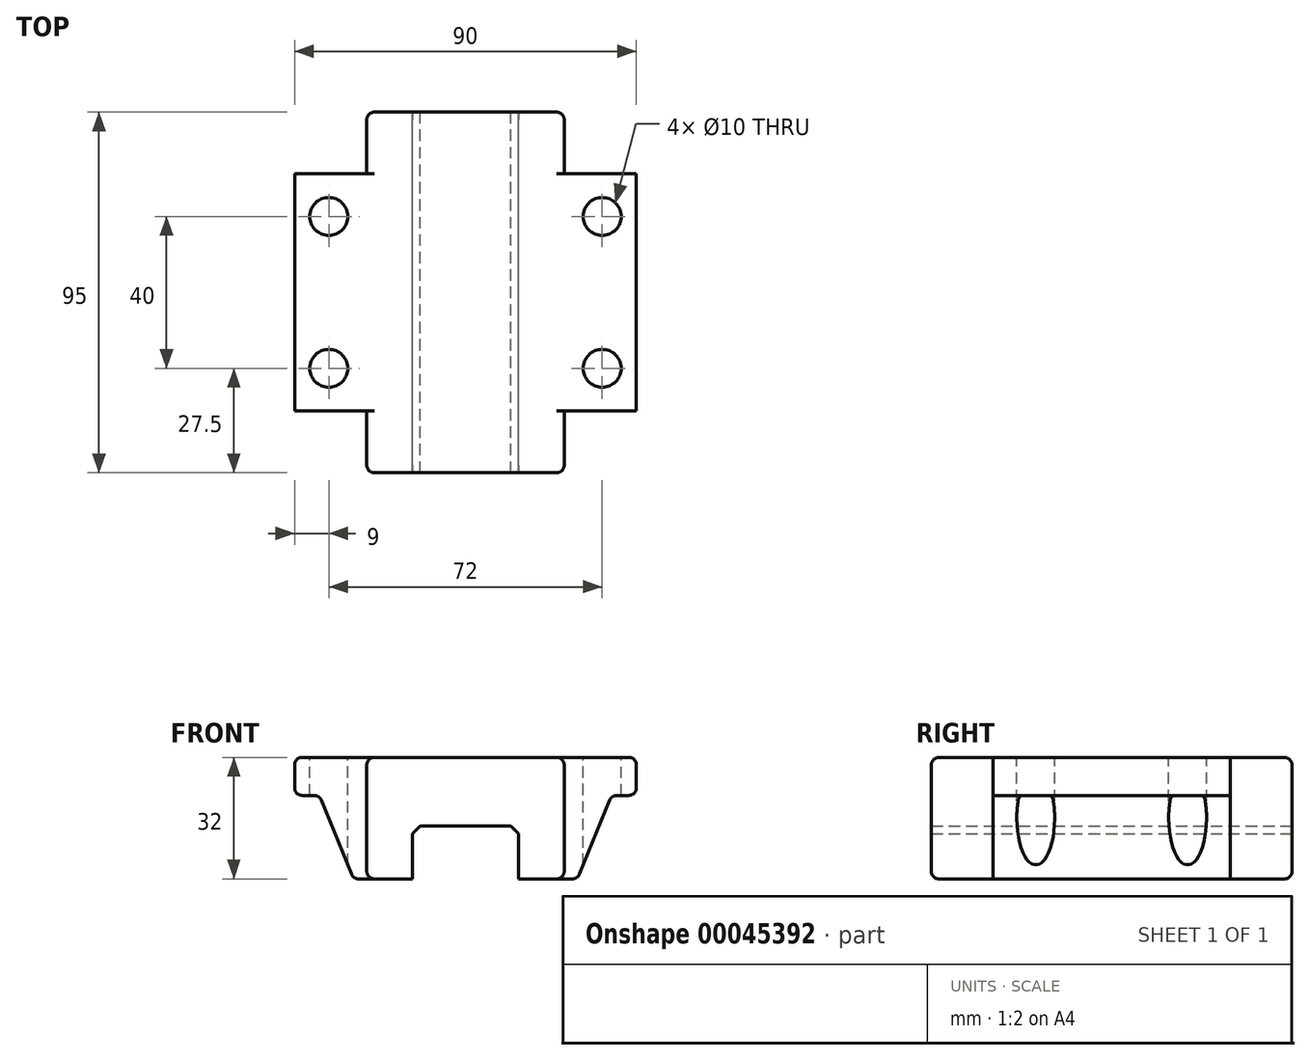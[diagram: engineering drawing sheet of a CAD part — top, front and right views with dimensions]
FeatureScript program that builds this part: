
annotation { "Feature Type Name" : "Feature", "Feature Type Description" : "" }
export const myFeature = defineFeature(function(context is Context, id is Id, definition is map)
    precondition{}
    {
        {
            var Q0;
            Q0=qCreatedBy(makeId("Front.planeOp"),FACE);
            var sketch = newSketch(context, id + "F0", { "sketchPlane" : qUnion([Q0])});
            skLineSegment(sketch, "E0.bottom", {"start": v(-47.43, 10.94) * mm, "end": v(42.57, 10.94) * mm});
            skLineSegment(sketch, "E0.top", {"start": v(-47.43, -21.06) * mm, "end": v(42.57, -21.06) * mm});
            skLineSegment(sketch, "E0.left", {"start": v(-47.43, 10.94) * mm, "end": v(-47.43, -21.06) * mm});
            skLineSegment(sketch, "E0.right", {"start": v(42.57, 10.94) * mm, "end": v(42.57, -21.06) * mm});
            skSolve(sketch);
        }
        {
            var Q0;
            Q0=qSketchRegion(id+"F0",true);
            extrude(context, id + "F1", {"entities" : qUnion([Q0]), "depth" : 65.2 * mm});
        }
        {
            var Q0;
            Q0=makeQuery(id+"F1.opExtrude","CAP_FACE",FACE,{"disambiguationData":[OSD([sQuery(id+"F0.wireOp",EDGE,"E0.bottom"),sQuery(id+"F0.wireOp",EDGE,"E0.top"),sQuery(id+"F0.wireOp",EDGE,"E0.left"),sQuery(id+"F0.wireOp",EDGE,"E0.right")])],"isStart":false});
            var sketch = newSketch(context, id + "F2", { "sketchPlane" : qUnion([Q0])});
            skLineSegment(sketch, "E1.bottom", {"start": v(-45.43, 10.94) * mm, "end": v(40.57, 10.94) * mm});
            skLineSegment(sketch, "E1.top", {"start": v(-45.43, 0.94) * mm, "end": v(-42.27, 0.94) * mm});
            skLineSegment(sketch, "E1.left", {"start": v(-47.43, 8.94) * mm, "end": v(-47.43, 2.94) * mm});
            skLineSegment(sketch, "E1.right", {"start": v(42.57, 8.94) * mm, "end": v(42.57, 2.94) * mm});
            skLineSegment(sketch, "E2.top", {"start": v(-30.59, -21.06) * mm, "end": v(25.73, -21.06) * mm});
            skLineSegment(sketch, "E3", {"start": v(-40.42, -0.3) * mm, "end": v(-32.44, -19.82) * mm});
            skLineSegment(sketch, "E4", {"start": v(27.58, -19.82) * mm, "end": v(35.56, -0.3) * mm});
            skLineSegment(sketch, "E5.trimOffspring", {"start": v(37.41, 0.94) * mm, "end": v(40.57, 0.94) * mm});
            skPoint(sketch, "E6.visualSharp", {"position": v(42.57, 0.94) * mm});
            skArc(sketch, "E6.filletArc", {"start": v(40.57, 0.94) * mm, "mid": v(41.98, 1.53) * mm, "end": v(42.57, 2.94) * mm});
            skPoint(sketch, "E7.visualSharp", {"position": v(42.57, 10.94) * mm});
            skArc(sketch, "E7.filletArc", {"start": v(42.57, 8.94) * mm, "mid": v(41.98, 10.36) * mm, "end": v(40.57, 10.94) * mm});
            skPoint(sketch, "E8.visualSharp", {"position": v(36.07, 0.94) * mm});
            skArc(sketch, "E8.filletArc", {"start": v(37.41, 0.94) * mm, "mid": v(36.3, 0.6) * mm, "end": v(35.56, -0.3) * mm});
            skPoint(sketch, "E9.visualSharp", {"position": v(27.07, -21.06) * mm});
            skArc(sketch, "E9.filletArc", {"start": v(25.73, -21.06) * mm, "mid": v(26.84, -20.72) * mm, "end": v(27.58, -19.82) * mm});
            skPoint(sketch, "E10.visualSharp", {"position": v(-31.93, -21.06) * mm});
            skArc(sketch, "E10.filletArc", {"start": v(-32.44, -19.82) * mm, "mid": v(-31.7, -20.72) * mm, "end": v(-30.59, -21.06) * mm});
            skPoint(sketch, "E11.visualSharp", {"position": v(-40.93, 0.94) * mm});
            skArc(sketch, "E11.filletArc", {"start": v(-40.42, -0.3) * mm, "mid": v(-41.16, 0.6) * mm, "end": v(-42.27, 0.94) * mm});
            skPoint(sketch, "E12.visualSharp", {"position": v(-47.43, 0.94) * mm});
            skArc(sketch, "E12.filletArc", {"start": v(-47.43, 2.94) * mm, "mid": v(-46.84, 1.53) * mm, "end": v(-45.43, 0.94) * mm});
            skPoint(sketch, "E13.visualSharp", {"position": v(-47.43, 10.94) * mm});
            skArc(sketch, "E13.filletArc", {"start": v(-45.43, 10.94) * mm, "mid": v(-46.84, 10.36) * mm, "end": v(-47.43, 8.94) * mm});
            skSolve(sketch);
        }
        {
            var Q0;
            Q0=qSketchRegion(id+"F2",true);
            extrude(context, id + "F3", {"entities" : qUnion([Q0]), "operationType" : NewBodyOperationType.ADD, "depth" : 25 * mm});
        }
        {
            var Q0;
            Q0=makeQuery(id+"F3.boolean.opBoolean","MERGE",FACE,{"derivedFrom":[makeQuery(id+"F1.opExtrude","SWEPT_FACE",FACE,{"disambiguationData":[OSD([sQuery(id+"F0.wireOp",EDGE,"E0.bottom")])]}),makeQuery(id+"F3.opExtrude","SWEPT_FACE",FACE,{"disambiguationData":[OSD([sQuery(id+"F2.wireOp",EDGE,"E1.bottom")])]})]});
            var sketch = newSketch(context, id + "F4", { "sketchPlane" : qUnion([Q0])});
            skLineSegment(sketch, "E14.bottom", {"start": v(-47.43, 0) * mm, "end": v(42.57, 0) * mm});
            skLineSegment(sketch, "E14.top", {"start": v(-47.43, -65.2) * mm, "end": v(42.57, -65.2) * mm});
            skLineSegment(sketch, "E14.left", {"start": v(-47.43, 0) * mm, "end": v(-47.43, -65.2) * mm});
            skLineSegment(sketch, "E14.right", {"start": v(42.57, 0) * mm, "end": v(42.57, -65.2) * mm});
            skSolve(sketch);
        }
        {
            var Q0;
            Q0=qSketchRegion(id+"F4",true);
            extrude(context, id + "F5", {"entities" : qUnion([Q0]), "operationType" : NewBodyOperationType.REMOVE, "endBound" : BoundingType.THROUGH_ALL, "oppositeDirection" : true, "depth" : 25 * mm});
        }
        {
            var Q0;
            Q0=makeQuery(id+"F3.opExtrude","CAP_FACE",FACE,{"disambiguationData":[OSD([sQuery(id+"F2.wireOp",EDGE,"E1.bottom"),sQuery(id+"F2.wireOp",EDGE,"E1.top"),sQuery(id+"F2.wireOp",EDGE,"E1.left"),sQuery(id+"F2.wireOp",EDGE,"E1.right"),sQuery(id+"F2.wireOp",EDGE,"E2.top"),sQuery(id+"F2.wireOp",EDGE,"E3"),sQuery(id+"F2.wireOp",EDGE,"E4"),sQuery(id+"F2.wireOp",EDGE,"E5.trimOffspring"),sQuery(id+"F2.wireOp",EDGE,"E6.filletArc"),sQuery(id+"F2.wireOp",EDGE,"E7.filletArc"),sQuery(id+"F2.wireOp",EDGE,"E8.filletArc"),sQuery(id+"F2.wireOp",EDGE,"E9.filletArc"),sQuery(id+"F2.wireOp",EDGE,"E10.filletArc"),sQuery(id+"F2.wireOp",EDGE,"E11.filletArc"),sQuery(id+"F2.wireOp",EDGE,"E12.filletArc"),sQuery(id+"F2.wireOp",EDGE,"E13.filletArc")])],"isStart":false});
            extrude(context, id + "F6", {"entities" : qUnion([Q0]), "operationType" : NewBodyOperationType.ADD, "oppositeDirection" : true, "depth" : 62.5 * mm});
        }
        {
            var Q0;
            Q0=makeQuery(id+"F3.opExtrude","CAP_FACE",FACE,{"disambiguationData":[OSD([sQuery(id+"F2.wireOp",EDGE,"E1.bottom"),sQuery(id+"F2.wireOp",EDGE,"E1.top"),sQuery(id+"F2.wireOp",EDGE,"E1.left"),sQuery(id+"F2.wireOp",EDGE,"E1.right"),sQuery(id+"F2.wireOp",EDGE,"E2.top"),sQuery(id+"F2.wireOp",EDGE,"E3"),sQuery(id+"F2.wireOp",EDGE,"E4"),sQuery(id+"F2.wireOp",EDGE,"E5.trimOffspring"),sQuery(id+"F2.wireOp",EDGE,"E6.filletArc"),sQuery(id+"F2.wireOp",EDGE,"E7.filletArc"),sQuery(id+"F2.wireOp",EDGE,"E8.filletArc"),sQuery(id+"F2.wireOp",EDGE,"E9.filletArc"),sQuery(id+"F2.wireOp",EDGE,"E10.filletArc"),sQuery(id+"F2.wireOp",EDGE,"E11.filletArc"),sQuery(id+"F2.wireOp",EDGE,"E12.filletArc"),sQuery(id+"F2.wireOp",EDGE,"E13.filletArc")])],"isStart":false});
            var sketch = newSketch(context, id + "F7", { "sketchPlane" : qUnion([Q0])});
            skLineSegment(sketch, "E15.bottom", {"start": v(-26.43, 10.94) * mm, "end": v(21.57, 10.94) * mm});
            skLineSegment(sketch, "E15.top", {"start": v(-26.43, -21.06) * mm, "end": v(-16.43, -21.06) * mm});
            skLineSegment(sketch, "E15.left", {"start": v(-28.43, 8.94) * mm, "end": v(-28.43, -19.06) * mm});
            skLineSegment(sketch, "E15.right", {"start": v(23.57, 8.94) * mm, "end": v(23.57, -19.06) * mm});
            skPoint(sketch, "E16.visualSharp", {"position": v(-28.43, 10.94) * mm});
            skArc(sketch, "E16.filletArc", {"start": v(-26.43, 10.94) * mm, "mid": v(-27.84, 10.36) * mm, "end": v(-28.43, 8.94) * mm});
            skPoint(sketch, "E17.visualSharp", {"position": v(23.57, 10.94) * mm});
            skArc(sketch, "E17.filletArc", {"start": v(23.57, 8.94) * mm, "mid": v(22.98, 10.36) * mm, "end": v(21.57, 10.94) * mm});
            skPoint(sketch, "E18.visualSharp", {"position": v(23.57, -21.06) * mm});
            skArc(sketch, "E18.filletArc", {"start": v(21.57, -21.06) * mm, "mid": v(22.98, -20.47) * mm, "end": v(23.57, -19.06) * mm});
            skPoint(sketch, "E19.visualSharp", {"position": v(-28.43, -21.06) * mm});
            skArc(sketch, "E19.filletArc", {"start": v(-28.43, -19.06) * mm, "mid": v(-27.84, -20.47) * mm, "end": v(-26.43, -21.06) * mm});
            skLineSegment(sketch, "E20.top", {"start": v(-14.3, -7.06) * mm, "end": v(9.45, -7.06) * mm});
            skLineSegment(sketch, "E20.left", {"start": v(-16.43, -21.06) * mm, "end": v(-16.43, -9.18) * mm});
            skLineSegment(sketch, "E20.right", {"start": v(11.57, -21.06) * mm, "end": v(11.57, -9.18) * mm});
            skLineSegment(sketch, "E21", {"start": v(-16.43, -9.18) * mm, "end": v(-14.3, -7.06) * mm});
            skLineSegment(sketch, "E22", {"start": v(9.45, -7.06) * mm, "end": v(11.57, -9.18) * mm});
            skLineSegment(sketch, "E23.trimOffspring", {"start": v(11.57, -21.06) * mm, "end": v(21.57, -21.06) * mm});
            skSolve(sketch);
        }
        {
            var Q0;
            Q0=makeQuery(id+"F7.imprint","IMPRINT",FACE,{"disambiguationData":[TD([[makeQuery(id+"F7.imprint","IMPRINT",EDGE,{"derivedFrom":sQuery(id+"F7.wireOp",EDGE,"E15.bottom")}),-1.0]])]});
            extrude(context, id + "F8", {"entities" : qUnion([Q0]), "operationType" : NewBodyOperationType.ADD, "depth" : 16.25 * mm, "hasSecondDirection" : true, "secondDirectionOppositeDirection" : true, "secondDirectionDepth" : 78.75 * mm});
        }
        {
            var Q0;
            Q0=makeQuery(id+"F8.opExtrude","CAP_EDGE",EDGE,{"disambiguationData":[OSD([sQuery(id+"F7.wireOp",EDGE,"E15.left")])],"isStart":false});
            var Q1;
            Q1=makeQuery(id+"F8.opExtrude","CAP_EDGE",EDGE,{"disambiguationData":[OSD([sQuery(id+"F7.wireOp",EDGE,"E15.bottom")])],"isStart":true});
            fillet(context, id + "F9", {"entities" : qUnion([Q0, Q1]), "radius" : 2 * mm, "tangentPropagation" : true, "allowEdgeOverflow" : false});
        }
        {
            var Q0;
            {var subQ0=sQuery(id+"F2.wireOp",EDGE,"E2.top");Q0=makeQuery(id+"F8.boolean.opBoolean","SPLIT",FACE,{"disambiguationData":[TD([makeQuery(id+"F8.opExtrude","SWEPT_FACE",FACE,{"disambiguationData":[OSD([sQuery(id+"F7.wireOp",EDGE,"E20.top")])]})])],"derivedFrom":makeQuery(id+"F3.opExtrude","CAP_FACE",FACE,{"disambiguationData":[OSD([sQuery(id+"F2.wireOp",EDGE,"E1.bottom"),sQuery(id+"F2.wireOp",EDGE,"E1.top"),sQuery(id+"F2.wireOp",EDGE,"E1.left"),sQuery(id+"F2.wireOp",EDGE,"E1.right"),subQ0,sQuery(id+"F2.wireOp",EDGE,"E3"),sQuery(id+"F2.wireOp",EDGE,"E4"),sQuery(id+"F2.wireOp",EDGE,"E5.trimOffspring"),sQuery(id+"F2.wireOp",EDGE,"E6.filletArc"),sQuery(id+"F2.wireOp",EDGE,"E7.filletArc"),sQuery(id+"F2.wireOp",EDGE,"E8.filletArc"),sQuery(id+"F2.wireOp",EDGE,"E9.filletArc"),sQuery(id+"F2.wireOp",EDGE,"E10.filletArc"),sQuery(id+"F2.wireOp",EDGE,"E11.filletArc"),sQuery(id+"F2.wireOp",EDGE,"E12.filletArc"),sQuery(id+"F2.wireOp",EDGE,"E13.filletArc")])],"isStart":false})});}
            var sketch = newSketch(context, id + "F10", { "sketchPlane" : qUnion([Q0])});
            skLineSegment(sketch, "E24", {"start": v(-16.43, -21.06) * mm, "end": v(-16.43, -9.18) * mm});
            skLineSegment(sketch, "E25", {"start": v(-16.43, -9.18) * mm, "end": v(-14.3, -7.06) * mm});
            skLineSegment(sketch, "E26", {"start": v(-14.3, -7.06) * mm, "end": v(9.45, -7.06) * mm});
            skLineSegment(sketch, "E27", {"start": v(9.45, -7.06) * mm, "end": v(11.57, -9.18) * mm});
            skLineSegment(sketch, "E28", {"start": v(11.57, -9.18) * mm, "end": v(11.57, -21.06) * mm});
            skLineSegment(sketch, "E29", {"start": v(11.57, -21.06) * mm, "end": v(-16.43, -21.06) * mm});
            skSolve(sketch);
        }
        {
            var Q0;
            Q0=qSketchRegion(id+"F10",true);
            extrude(context, id + "F11", {"entities" : qUnion([Q0]), "operationType" : NewBodyOperationType.REMOVE, "endBound" : BoundingType.THROUGH_ALL, "oppositeDirection" : true, "depth" : 25 * mm});
        }
        {
            var Q0;
            {var subQ0=sQuery(id+"F2.wireOp",EDGE,"E1.bottom");Q0=makeQuery(id+"F8.boolean.opBoolean","MERGE",FACE,{"derivedFrom":[makeQuery(id+"F6.boolean.opBoolean","MERGE",FACE,{"derivedFrom":[makeQuery(id+"F3.boolean.opBoolean","MERGE",FACE,{"derivedFrom":[makeQuery(id+"F1.opExtrude","SWEPT_FACE",FACE,{"disambiguationData":[OSD([sQuery(id+"F0.wireOp",EDGE,"E0.bottom")])]}),makeQuery(id+"F3.opExtrude","SWEPT_FACE",FACE,{"disambiguationData":[OSD([subQ0])]})]}),makeQuery(id+"F6.opExtrude","SWEPT_FACE",FACE,{"disambiguationData":[OSD([subQ0])]})]}),makeQuery(id+"F8.opExtrude","SWEPT_FACE",FACE,{"disambiguationData":[OSD([sQuery(id+"F7.wireOp",EDGE,"E15.bottom")])]})]});}
            var sketch = newSketch(context, id + "F12", { "sketchPlane" : qUnion([Q0])});
            skCircle(sketch, "E30", {"center": v(-38.43, -38.95) * mm, "radius": 5 * mm});
            skCircle(sketch, "E31", {"center": v(-38.43, -78.95) * mm, "radius": 5 * mm});
            skCircle(sketch, "E32", {"center": v(33.57, -78.95) * mm, "radius": 5 * mm});
            skCircle(sketch, "E33", {"center": v(33.57, -38.95) * mm, "radius": 5 * mm});
            skSolve(sketch);
        }
        {
            var Q0;
            Q0 = qSketchRegion(id + "F12", true);
            extrude(context, id + "F13", {"entities" : qUnion([Q0]), "operationType" : NewBodyOperationType.REMOVE, "endBound" : BoundingType.THROUGH_ALL, "oppositeDirection" : true, "depth" : 25 * mm});
        }
    });
